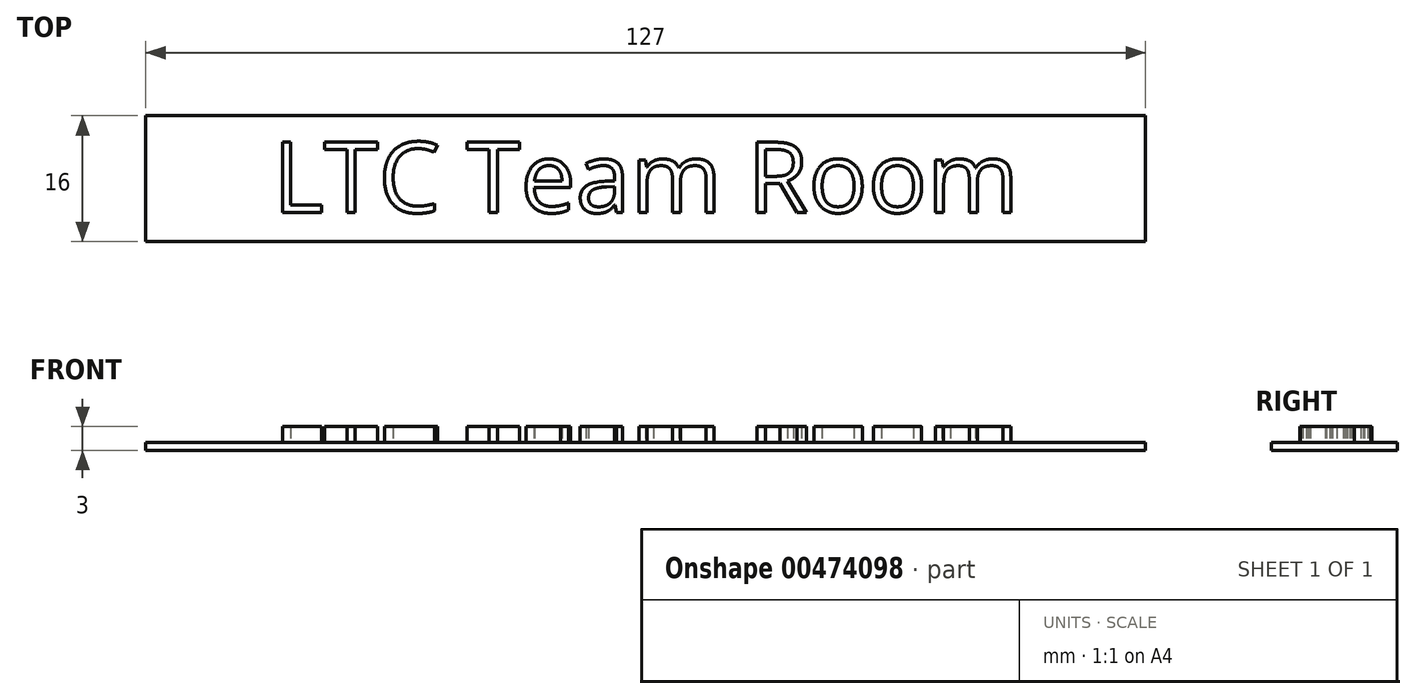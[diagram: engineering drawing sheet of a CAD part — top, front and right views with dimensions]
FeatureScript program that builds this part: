
annotation { "Feature Type Name" : "Feature", "Feature Type Description" : "" }
export const myFeature = defineFeature(function(context is Context, id is Id, definition is map)
    precondition{}
    {
        {
            var Q0;
            Q0=qCreatedBy(makeId("Top.planeOp"),FACE);
            var sketch = newSketch(context, id + "F0", { "sketchPlane" : qUnion([Q0])});
            skLineSegment(sketch, "E0.bottom", {"start": v(-63.5, 8) * mm, "end": v(63.5, 8) * mm});
            skLineSegment(sketch, "E0.top", {"start": v(-63.5, -8) * mm, "end": v(63.5, -8) * mm});
            skLineSegment(sketch, "E0.left", {"start": v(-63.5, 8) * mm, "end": v(-63.5, -8) * mm});
            skLineSegment(sketch, "E0.right", {"start": v(63.5, 8) * mm, "end": v(63.5, -8) * mm});
            skPoint(sketch, "E0.middle", {"position": v(0, 0) * mm});
            skSolve(sketch);
        }
        {
            var Q0;
            Q0 = qSketchRegion(id + "F0", true);
            extrude(context, id + "F1", {"entities" : qUnion([Q0]), "depth" : 1 * mm});
        }
        {
            var Q0;
            Q0=makeQuery(id+"F1.opExtrude","CAP_FACE",FACE,{"disambiguationData":[OSD([sQuery(id+"F0.wireOp",EDGE,"E0.bottom"),sQuery(id+"F0.wireOp",EDGE,"E0.top"),sQuery(id+"F0.wireOp",EDGE,"E0.left"),sQuery(id+"F0.wireOp",EDGE,"E0.right")])],"isStart":false});
            var sketch = newSketch(context, id + "F2", { "sketchPlane" : qUnion([Q0])});
            skText(sketch, "E1", { "text": "LTC Team Room", "fontName": "OpenSans-Regular.ttf"});
            const initialGuessF2  = {"E1": [-0.04735, -0.0043, 1, 0, 0.009]};
            skSetInitialGuess(sketch, initialGuessF2);
            skSolve(sketch);
        }
        {
            var Q0;
            Q0 = qSketchRegion(id + "F2", true);
            extrude(context, id + "F3", {"entities" : qUnion([Q0]), "operationType" : NewBodyOperationType.ADD, "depth" : 2 * mm});
        }
    });
